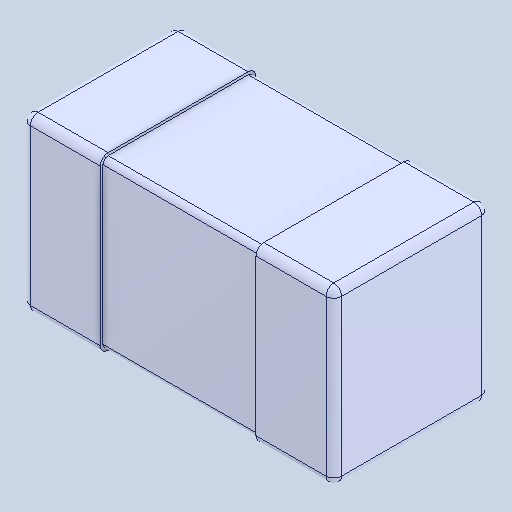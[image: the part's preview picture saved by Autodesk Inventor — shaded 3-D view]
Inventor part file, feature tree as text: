
AUTODESK INVENTOR PART (.ipt)
format: ipt  version: 2025 (Build 290162000, 162)  size: 130,560 bytes
history: native  units: mm
features: fillet x1, mirror x1, other x1
ambient origin geometry x8: Origin, YZ Plane, XZ Plane, XY Plane, X Axis, Y Axis, Z Axis, Center Point
bodies: Solid1 (feature_tree), Solid2 (feature_tree), Solid3 (feature_tree)
feature tree (3):
  fillet  "Fillet1"  [1 undecoded]
  mirror  "Mirror2"
  other  "Boss-Extrude2"
note: 1 required parameter value undecoded (feature->parameter linkage not recoverable at this tier; creation-order binding heuristic only, values carry confidence <= 0.55)
